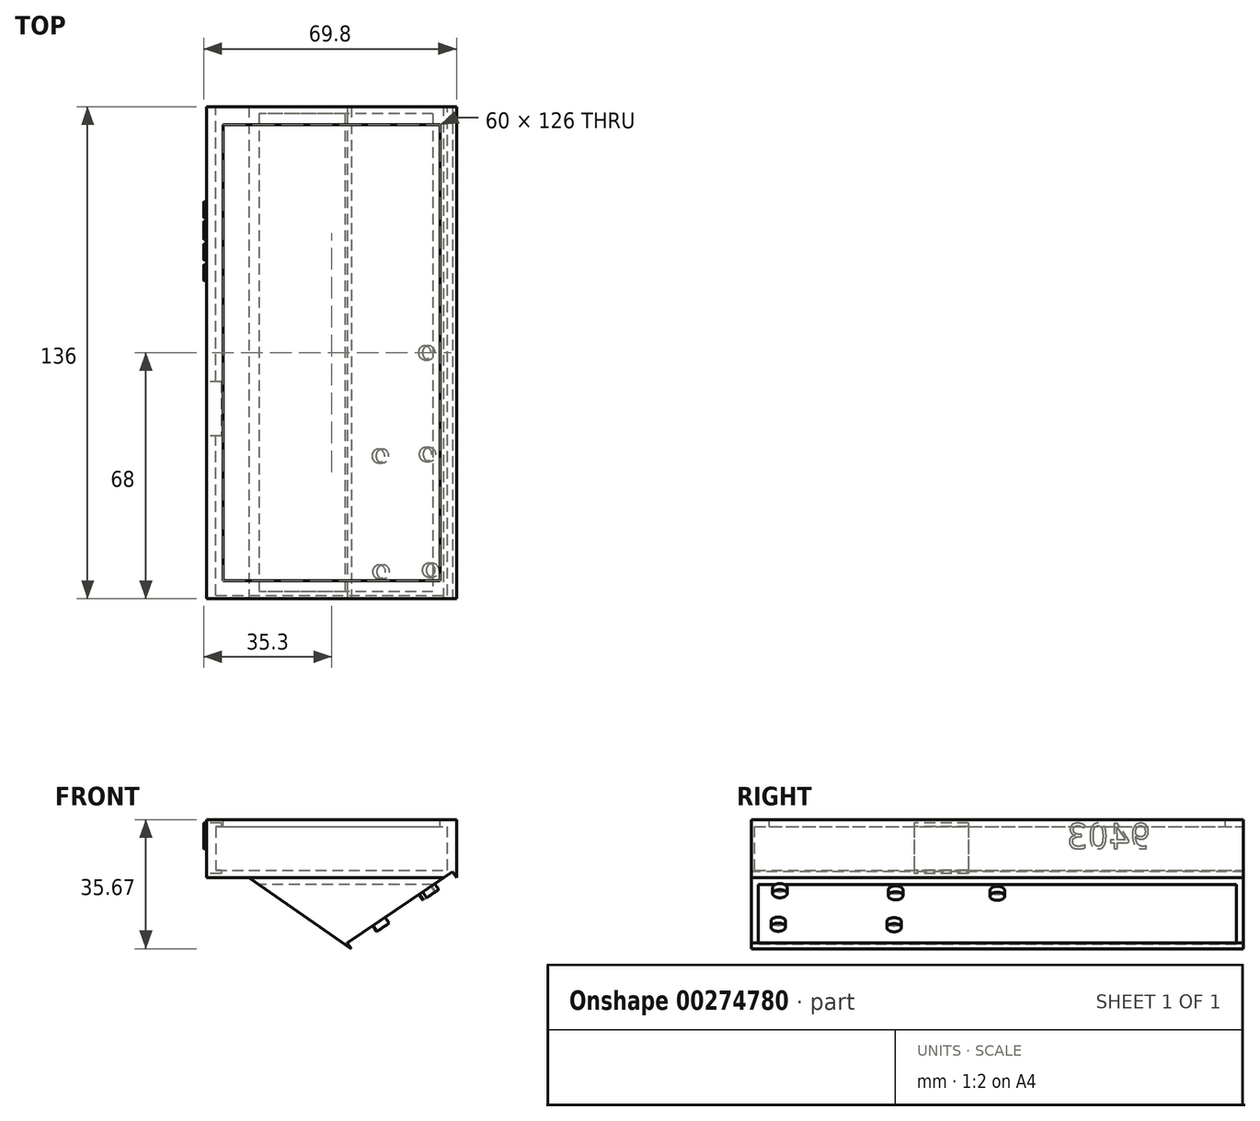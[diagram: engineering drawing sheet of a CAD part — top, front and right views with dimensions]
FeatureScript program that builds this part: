
annotation { "Feature Type Name" : "Feature", "Feature Type Description" : "" }
export const myFeature = defineFeature(function(context is Context, id is Id, definition is map)
    precondition{}
    {
        {
            var Q0;
            Q0=qCreatedBy(makeId("Top.planeOp"),FACE);
            var sketch = newSketch(context, id + "F0", { "sketchPlane" : qUnion([Q0])});
            skLineSegment(sketch, "E0.bottom", {"start": v(34.5, 68) * mm, "end": v(-34.5, 68) * mm});
            skLineSegment(sketch, "E0.top", {"start": v(34.5, -68) * mm, "end": v(-34.5, -68) * mm});
            skLineSegment(sketch, "E0.left", {"start": v(34.5, 68) * mm, "end": v(34.5, -68) * mm});
            skLineSegment(sketch, "E0.right", {"start": v(-34.5, 68) * mm, "end": v(-34.5, -68) * mm});
            skPoint(sketch, "E0.middle", {"position": v(0, 0) * mm});
            skSolve(sketch);
        }
        {
            var Q0;
            Q0=qSketchRegion(id+"F0",true);
            extrude(context, id + "F1", {"entities" : qUnion([Q0]), "endBound" : BoundingType.SYMMETRIC, "depth" : 16 * mm});
        }
        {
            var Q0;
            Q0=makeQuery(id+"F1.opExtrude","SWEPT_FACE",FACE,{"disambiguationData":[OSD([sQuery(id+"F0.wireOp",EDGE,"E0.top")])]});
            var sketch = newSketch(context, id + "F2", { "sketchPlane" : qUnion([Q0])});
            skLineSegment(sketch, "E1", {"start": v(34.5, -8) * mm, "end": v(5.46, -27.67) * mm});
            skLineSegment(sketch, "E2", {"start": v(5.46, -27.67) * mm, "end": v(-22.9, -8) * mm});
            skSolve(sketch);
        }
        {
            var Q0;
            Q0=qSketchRegion(id+"F2",true);
            var Q1;
            {var subQ0=sQuery(id+"F2.wireOp",EDGE,"E1");Q1=makeQuery(id+"F2.imprint","IMPRINT",FACE,{"disambiguationData":[TD([[makeQuery(id+"F2.imprint","IMPRINT",EDGE,{"derivedFrom":subQ0}),-1.0]])]});}
            extrude(context, id + "F3", {"entities" : qUnion([Q0, Q1]), "oppositeDirection" : true, "depth" : 136 * mm});
        }
        {
            var Q0;
            Q0=makeQuery(id+"F1.opExtrude","CAP_FACE",FACE,{"disambiguationData":[OSD([sQuery(id+"F0.wireOp",EDGE,"E0.bottom"),sQuery(id+"F0.wireOp",EDGE,"E0.top"),sQuery(id+"F0.wireOp",EDGE,"E0.left"),sQuery(id+"F0.wireOp",EDGE,"E0.right")])],"isStart":false});
            var sketch = newSketch(context, id + "F4", { "sketchPlane" : qUnion([Q0])});
            skLineSegment(sketch, "E3.bottom", {"start": v(30, 63) * mm, "end": v(-30, 63) * mm});
            skLineSegment(sketch, "E3.top", {"start": v(30, -63) * mm, "end": v(-30, -63) * mm});
            skLineSegment(sketch, "E3.left", {"start": v(30, 63) * mm, "end": v(30, -63) * mm});
            skLineSegment(sketch, "E3.right", {"start": v(-30, 63) * mm, "end": v(-30, -63) * mm});
            skPoint(sketch, "E3.middle", {"position": v(0, 0) * mm});
            skSolve(sketch);
        }
        {
            var Q0;
            Q0=makeQuery(id+"F4.imprint","IMPRINT",FACE,{"disambiguationData":[TD([[makeQuery(id+"F4.imprint","IMPRINT",EDGE,{"derivedFrom":sQuery(id+"F4.wireOp",EDGE,"E3.bottom")}),1.0]])]});
            extrude(context, id + "F5", {"entities" : qUnion([Q0]), "operationType" : NewBodyOperationType.REMOVE, "oppositeDirection" : true, "depth" : 14 * mm});
        }
        {
            var Q0;
            Q0=makeQuery(id+"F1.opExtrude","SWEPT_FACE",FACE,{"disambiguationData":[OSD([sQuery(id+"F0.wireOp",EDGE,"E0.bottom")])]});
            var sketch = newSketch(context, id + "F6", { "sketchPlane" : qUnion([Q0])});
            skLineSegment(sketch, "E4.bottom", {"start": v(32, -6) * mm, "end": v(-32, -6) * mm});
            skLineSegment(sketch, "E4.top", {"start": v(32, 6) * mm, "end": v(-32, 6) * mm});
            skLineSegment(sketch, "E4.left", {"start": v(32, -6) * mm, "end": v(32, 6) * mm});
            skLineSegment(sketch, "E4.right", {"start": v(-32, -6) * mm, "end": v(-32, 6) * mm});
            skPoint(sketch, "E4.middle", {"position": v(0, 0) * mm});
            skSolve(sketch);
        }
        {
            var Q0;
            Q0=qSketchRegion(id+"F6",true);
            extrude(context, id + "F7", {"entities" : qUnion([Q0]), "operationType" : NewBodyOperationType.REMOVE, "oppositeDirection" : true, "depth" : 135 * mm});
        }
        {
            var Q0;
            Q0=makeQuery(id+"F3.opExtrude","SWEPT_FACE",FACE,{"disambiguationData":[OSD([sQuery(id+"F2.wireOp",EDGE,"E2")])]});
            shell(context, id + "F8", {"entities" : qUnion([Q0]), "thickness" : 2 * mm});
        }
        {
            var Q0;
            Q0=makeQuery(id+"F3.opExtrude","SWEPT_FACE",FACE,{"disambiguationData":[OSD([sQuery(id+"F2.wireOp",EDGE,"E1")])]});
            var sketch = newSketch(context, id + "F9", { "sketchPlane" : qUnion([Q0])});
            skCircle(sketch, "E5", {"center": v(14.83, 0) * mm, "radius": 2 * mm});
            skCircle(sketch, "E6", {"center": v(-1.17, 0) * mm, "radius": 2 * mm});
            skLineSegment(sketch, "E7", {"start": v(-1.17, 0) * mm, "end": v(0, -68) * mm, "construction": true});
            skLineSegment(sketch, "E8", {"start": v(14.83, 0) * mm, "end": v(16, -68) * mm, "construction": true});
            skCircle(sketch, "E9", {"center": v(-0.64, -28.53) * mm, "radius": 2 * mm});
            skCircle(sketch, "E10", {"center": v(15.08, -28.09) * mm, "radius": 2 * mm});
            skCircle(sketch, "E11", {"center": v(-0.4, -60.53) * mm, "radius": 2 * mm});
            skCircle(sketch, "E12", {"center": v(16.12, -60.07) * mm, "radius": 2 * mm});
            skLineSegment(sketch, "E13.MirrorCS", {"start": v(-1.17, 0) * mm, "end": v(0, 68) * mm, "construction": true});
            skCircle(sketch, "E14.MirrorC", {"center": v(-0.64, 28.53) * mm, "radius": 2 * mm});
            skLineSegment(sketch, "E15.MirrorCS", {"start": v(14.83, 0) * mm, "end": v(16, 68) * mm, "construction": true});
            skCircle(sketch, "E16.MirrorC", {"center": v(15.08, 28.09) * mm, "radius": 2 * mm});
            skCircle(sketch, "E17.MirrorC", {"center": v(-0.4, 60.53) * mm, "radius": 2 * mm});
            skCircle(sketch, "E18.MirrorC", {"center": v(16.12, 60.07) * mm, "radius": 2 * mm});
            skSolve(sketch);
        }
        {
            var Q0;
            Q0=makeQuery(id+"F9.imprint","IMPRINT",FACE,{"disambiguationData":[TD([[makeQuery(id+"F9.imprint","IMPRINT",EDGE,{"derivedFrom":sQuery(id+"F9.wireOp",EDGE,"E5")}),-1.0]])]});
            var Q1;
            Q1=makeQuery(id+"F9.imprint","IMPRINT",FACE,{"disambiguationData":[TD([[makeQuery(id+"F9.imprint","IMPRINT",EDGE,{"derivedFrom":sQuery(id+"F9.wireOp",EDGE,"E14.MirrorC")}),-1.0]])]});
            var Q2;
            Q2=makeQuery(id+"F9.imprint","IMPRINT",FACE,{"disambiguationData":[TD([[makeQuery(id+"F9.imprint","IMPRINT",EDGE,{"derivedFrom":sQuery(id+"F9.wireOp",EDGE,"E16.MirrorC")}),-1.0]])]});
            var Q3;
            Q3=makeQuery(id+"F9.imprint","IMPRINT",FACE,{"disambiguationData":[TD([[makeQuery(id+"F9.imprint","IMPRINT",EDGE,{"derivedFrom":sQuery(id+"F9.wireOp",EDGE,"E17.MirrorC")}),-1.0]])]});
            var Q4;
            Q4=makeQuery(id+"F9.imprint","IMPRINT",FACE,{"disambiguationData":[TD([[makeQuery(id+"F9.imprint","IMPRINT",EDGE,{"derivedFrom":sQuery(id+"F9.wireOp",EDGE,"E18.MirrorC")}),-1.0]])]});
            var Q5;
            Q5=makeQuery(id+"F9.imprint","IMPRINT",FACE,{"disambiguationData":[TD([[makeQuery(id+"F9.imprint","IMPRINT",EDGE,{"derivedFrom":sQuery(id+"F9.wireOp",EDGE,"E6")}),1.0]])]});
            var Q6;
            Q6=makeQuery(id+"F9.imprint","IMPRINT",FACE,{"disambiguationData":[TD([[makeQuery(id+"F9.imprint","IMPRINT",EDGE,{"derivedFrom":sQuery(id+"F9.wireOp",EDGE,"E9")}),1.0]])]});
            var Q7;
            Q7=makeQuery(id+"F9.imprint","IMPRINT",FACE,{"disambiguationData":[TD([[makeQuery(id+"F9.imprint","IMPRINT",EDGE,{"derivedFrom":sQuery(id+"F9.wireOp",EDGE,"E10")}),1.0]])]});
            var Q8;
            Q8=makeQuery(id+"F9.imprint","IMPRINT",FACE,{"disambiguationData":[TD([[makeQuery(id+"F9.imprint","IMPRINT",EDGE,{"derivedFrom":sQuery(id+"F9.wireOp",EDGE,"E12")}),1.0]])]});
            var Q9;
            Q9=makeQuery(id+"F9.imprint","IMPRINT",FACE,{"disambiguationData":[TD([[makeQuery(id+"F9.imprint","IMPRINT",EDGE,{"derivedFrom":sQuery(id+"F9.wireOp",EDGE,"E11")}),1.0]])]});
            extrude(context, id + "F10", {"entities" : qUnion([Q0, Q1, Q2, Q3, Q4, Q5, Q6, Q7, Q8, Q9]), "operationType" : NewBodyOperationType.REMOVE, "oppositeDirection" : true, "depth" : 2 * mm});
        }
        {
            var Q0;
            Q0=makeQuery(id+"F1.opExtrude","SWEPT_FACE",FACE,{"disambiguationData":[OSD([sQuery(id+"F0.wireOp",EDGE,"E0.right")])]});
            var sketch = newSketch(context, id + "F11", { "sketchPlane" : qUnion([Q0])});
            skText(sketch, "E19", { "text": "9403", "fontName": "DroidSansMono.ttf"});
            const initialGuessF11  = {"E19": [-0.04242, 0, 1, 0, 0.007]};
            skSetInitialGuess(sketch, initialGuessF11);
            skSolve(sketch);
        }
        {
            var Q0;
            Q0=qSketchRegion(id+"F11",true);
            extrude(context, id + "F12", {"entities" : qUnion([Q0]), "operationType" : NewBodyOperationType.ADD, "depth" : 0.8 * mm});
        }
        {
            var Q0;
            {var subQ0=sQuery(id+"F0.wireOp",EDGE,"E0.right");var subQ3=sQuery(id+"F0.wireOp",EDGE,"E0.bottom");Q0=makeQuery(id+"F12.boolean.opBoolean","SPLIT",FACE,{"disambiguationData":[TD([makeQuery(id+"F1.opExtrude","SWEPT_FACE",FACE,{"disambiguationData":[OSD([subQ3])]})])],"derivedFrom":makeQuery(id+"F1.opExtrude","SWEPT_FACE",FACE,{"disambiguationData":[OSD([subQ0])]})});}
            var sketch = newSketch(context, id + "F13", { "sketchPlane" : qUnion([Q0])});
            skLineSegment(sketch, "E20.bottom", {"start": v(8, 7.08) * mm, "end": v(23, 7.08) * mm});
            skLineSegment(sketch, "E20.top", {"start": v(8, -6.92) * mm, "end": v(23, -6.92) * mm});
            skLineSegment(sketch, "E20.left", {"start": v(8, 7.08) * mm, "end": v(8, -6.92) * mm});
            skLineSegment(sketch, "E20.right", {"start": v(23, 7.08) * mm, "end": v(23, -6.92) * mm});
            skSolve(sketch);
        }
        {
            var Q0;
            Q0 = qSketchRegion(id + "F13", true);
            extrude(context, id + "F14", {"entities" : qUnion([Q0]), "operationType" : NewBodyOperationType.REMOVE, "oppositeDirection" : true, "depth" : 4 * mm});
        }
    });
